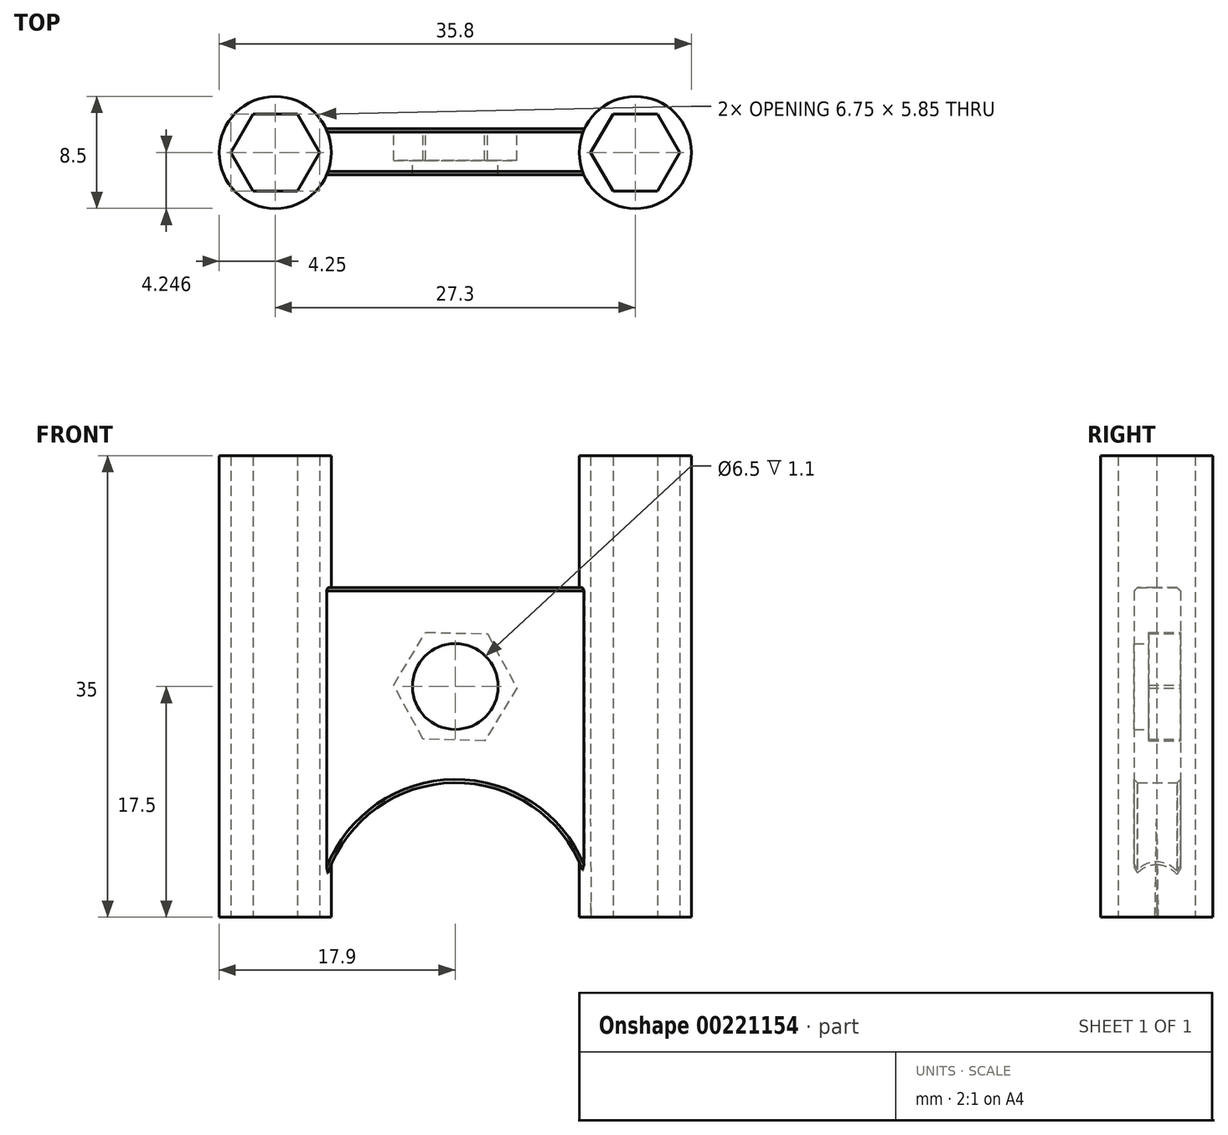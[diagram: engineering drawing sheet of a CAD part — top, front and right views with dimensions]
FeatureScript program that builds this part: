
annotation { "Feature Type Name" : "Feature", "Feature Type Description" : "" }
export const myFeature = defineFeature(function(context is Context, id is Id, definition is map)
    precondition{}
    {
        {
            var Q0;
            Q0=qCreatedBy(makeId("Front.planeOp"),FACE);
            var sketch = newSketch(context, id + "F0", { "sketchPlane" : qUnion([Q0])});
            skLineSegment(sketch, "E0.bottom", {"start": v(10.25, -7.5) * mm, "end": v(-10.25, -7.5) * mm});
            skLineSegment(sketch, "E0.top", {"start": v(10.25, 7.5) * mm, "end": v(-10.25, 7.5) * mm});
            skLineSegment(sketch, "E0.left", {"start": v(10.25, -7.5) * mm, "end": v(10.25, 7.5) * mm});
            skLineSegment(sketch, "E0.right", {"start": v(-10.25, -7.5) * mm, "end": v(-10.25, 7.5) * mm});
            skPoint(sketch, "E0.middle", {"position": v(0, 0) * mm});
            skCircle(sketch, "E1", {"center": v(0, 0) * mm, "radius": 3.25 * mm});
            skLineSegment(sketch, "E2", {"start": v(-10.25, -7.5) * mm, "end": v(-10.25, -17.5) * mm});
            skLineSegment(sketch, "E3", {"start": v(-10.25, -17.5) * mm, "end": v(10.34, -17.5) * mm});
            skLineSegment(sketch, "E4", {"start": v(10.34, -17.5) * mm, "end": v(10.25, -7.5) * mm});
            skArc(sketch, "E5", {"start": v(10.34, -17.5) * mm, "mid": v(0.04, -7.3) * mm, "end": v(-10.25, -17.5) * mm});
            skSolve(sketch);
        }
        {
            var Q0;
            Q0=makeQuery(id+"F0.imprint","IMPRINT",FACE,{"disambiguationData":[TD([[makeQuery(id+"F0.imprint","IMPRINT",EDGE,{"derivedFrom":sQuery(id+"F0.wireOp",EDGE,"E0.bottom")}),-1.0]])]});
            var Q1;
            Q1=makeQuery(id+"F0.imprint","IMPRINT",FACE,{"disambiguationData":[TD([[makeQuery(id+"F0.imprint","IMPRINT",EDGE,{"derivedFrom":sQuery(id+"F0.wireOp",EDGE,"E0.bottom")}),1.0]])]});
            extrude(context, id + "F1", {"entities" : qUnion([Q0, Q1]), "depth" : 3.5 * mm});
        }
        {
            var Q0;
            Q0=qCreatedBy(makeId("Front.planeOp"),FACE);
            var sketch = newSketch(context, id + "F2", { "sketchPlane" : qUnion([Q0])});
            skCircle(sketch, "E6.cCircle", {"center": v(0, 0) * mm, "radius": 4.68 * mm, "construction": true});
            skLineSegment(sketch, "E6.0", {"start": v(2.24, -4.1) * mm, "end": v(-2.44, -4) * mm});
            skLineSegment(sketch, "E6.1", {"start": v(-2.44, -4) * mm, "end": v(-4.68, 0.11) * mm});
            skLineSegment(sketch, "E6.2", {"start": v(-4.68, 0.11) * mm, "end": v(-2.24, 4.1) * mm});
            skLineSegment(sketch, "E6.3", {"start": v(-2.24, 4.1) * mm, "end": v(2.44, 4) * mm});
            skLineSegment(sketch, "E6.4", {"start": v(2.44, 4) * mm, "end": v(4.68, -0.11) * mm});
            skLineSegment(sketch, "E6.5", {"start": v(4.68, -0.11) * mm, "end": v(2.24, -4.1) * mm});
            skSolve(sketch);
        }
        {
            var Q0;
            Q0=qSketchRegion(id+"F2",true);
            extrude(context, id + "F3", {"entities" : qUnion([Q0]), "operationType" : NewBodyOperationType.REMOVE, "depth" : 2.4 * mm});
        }
        {
            var Q0;
            Q0=qCreatedBy(makeId("Top.planeOp"),FACE);
            var sketch = newSketch(context, id + "F4", { "sketchPlane" : qUnion([Q0])});
            skCircle(sketch, "E7", {"center": v(13.65, -1.8) * mm, "radius": 4.25 * mm});
            skCircle(sketch, "E8.MirrorC", {"center": v(-13.65, -1.8) * mm, "radius": 4.25 * mm});
            skCircle(sketch, "E9.cCircle", {"center": v(13.65, -1.8) * mm, "radius": 2.92 * mm, "construction": true});
            skLineSegment(sketch, "E9.0", {"start": v(15.34, -4.73) * mm, "end": v(11.96, -4.73) * mm});
            skLineSegment(sketch, "E9.1", {"start": v(11.96, -4.73) * mm, "end": v(10.27, -1.8) * mm});
            skLineSegment(sketch, "E9.2", {"start": v(10.27, -1.8) * mm, "end": v(11.96, 1.12) * mm});
            skLineSegment(sketch, "E9.3", {"start": v(11.96, 1.12) * mm, "end": v(15.34, 1.12) * mm});
            skLineSegment(sketch, "E9.4", {"start": v(15.34, 1.12) * mm, "end": v(17.03, -1.8) * mm});
            skLineSegment(sketch, "E9.5", {"start": v(17.03, -1.8) * mm, "end": v(15.34, -4.73) * mm});
            skPoint(sketch, "E9.0.midPoint", {"position": v(13.65, -4.73) * mm});
            skLineSegment(sketch, "E10.MirrorCS", {"start": v(-15.34, -4.73) * mm, "end": v(-11.96, -4.73) * mm});
            skLineSegment(sketch, "E11.MirrorCS", {"start": v(-11.96, -4.73) * mm, "end": v(-10.27, -1.8) * mm});
            skLineSegment(sketch, "E12.MirrorCS", {"start": v(-10.27, -1.8) * mm, "end": v(-11.96, 1.12) * mm});
            skLineSegment(sketch, "E13.MirrorCS", {"start": v(-11.96, 1.12) * mm, "end": v(-15.34, 1.12) * mm});
            skLineSegment(sketch, "E14.MirrorCS", {"start": v(-15.34, 1.12) * mm, "end": v(-17.03, -1.8) * mm});
            skLineSegment(sketch, "E15.MirrorCS", {"start": v(-17.03, -1.8) * mm, "end": v(-15.34, -4.73) * mm});
            skCircle(sketch, "E16.MirrorC", {"center": v(-13.65, -1.8) * mm, "radius": 2.92 * mm, "construction": true});
            skSolve(sketch);
        }
        {
            var Q0;
            Q0=qSketchRegion(id+"F4",true);
            extrude(context, id + "F5", {"entities" : qUnion([Q0]), "operationType" : NewBodyOperationType.ADD, "depth" : 17.5 * mm, "hasSecondDirection" : true, "secondDirectionOppositeDirection" : true, "secondDirectionDepth" : 17.5 * mm});
        }
        {
            var Q0;
            Q0=makeQuery(id+"F1.opExtrude","CAP_EDGE",EDGE,{"disambiguationData":[OSD([sQuery(id+"F0.wireOp",EDGE,"E0.top")])],"isStart":false});
            var Q1;
            Q1=makeQuery(id+"F1.opExtrude","CAP_EDGE",EDGE,{"disambiguationData":[OSD([sQuery(id+"F0.wireOp",EDGE,"E0.top")])],"isStart":true});
            var Q2;
            Q2=makeQuery(id+"F1.opExtrude","CAP_EDGE",EDGE,{"disambiguationData":[OSD([sQuery(id+"F0.wireOp",EDGE,"E5")])],"isStart":false});
            var Q3;
            Q3=makeQuery(id+"F1.opExtrude","CAP_EDGE",EDGE,{"disambiguationData":[OSD([sQuery(id+"F0.wireOp",EDGE,"E5")])],"isStart":true});
            chamfer(context, id + "F6", {"entities" : qUnion([Q0, Q1, Q2, Q3]), "width" : .25 * mm, "tangentPropagation" : true});
        }
    });
